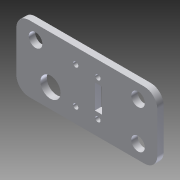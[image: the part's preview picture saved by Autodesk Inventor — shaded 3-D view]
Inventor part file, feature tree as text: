
AUTODESK INVENTOR PART (.ipt)
format: ipt  version: 2014 SP1 (Build 180222100, 222)  size: 133,632 bytes
history: native  units: in
note: dims shown in document units (in); Inventor stores cm internally (conversion verified against a paired STEP export)
features: reference x7, extrude x2, sketch x2, fillet x1
ambient origin geometry x8: Origin, YZ Plane, XZ Plane, XY Plane, X Axis, Y Axis, Z Axis, Center Point
bodies: Solid1 (feature_tree)
feature tree (12):
  extrude  "Extrusion1"  Depth=1.3in
  fillet  "Fillet1"  Radius=0.375in
  extrude  "Extrusion2"  Depth=0.125in TaperAngle=0.0deg
  sketch  "Sketch1"  dims[d0=1.3in d1=0.375in d2=0.375in]
  reference  "Reference1"
  reference  "Reference2"
  reference  "Reference3"
  reference  "Reference4"
  reference  "Reference5"
  reference  "Reference6"
  reference  "Reference7"
  sketch  "Sketch2"  dims[d3=0.05in d4=0.125in d5=0.0in d6=0.25in d7=0.1024in d8=0.7874in d10=0.4331in d11=0.7874in d13=0.7087in d16=0.4724in d17=0.1378in d18=0.1575in d19=0.3937in d20=0.2756in d21=0.7087in d22=1.0in d23=0.0in]
